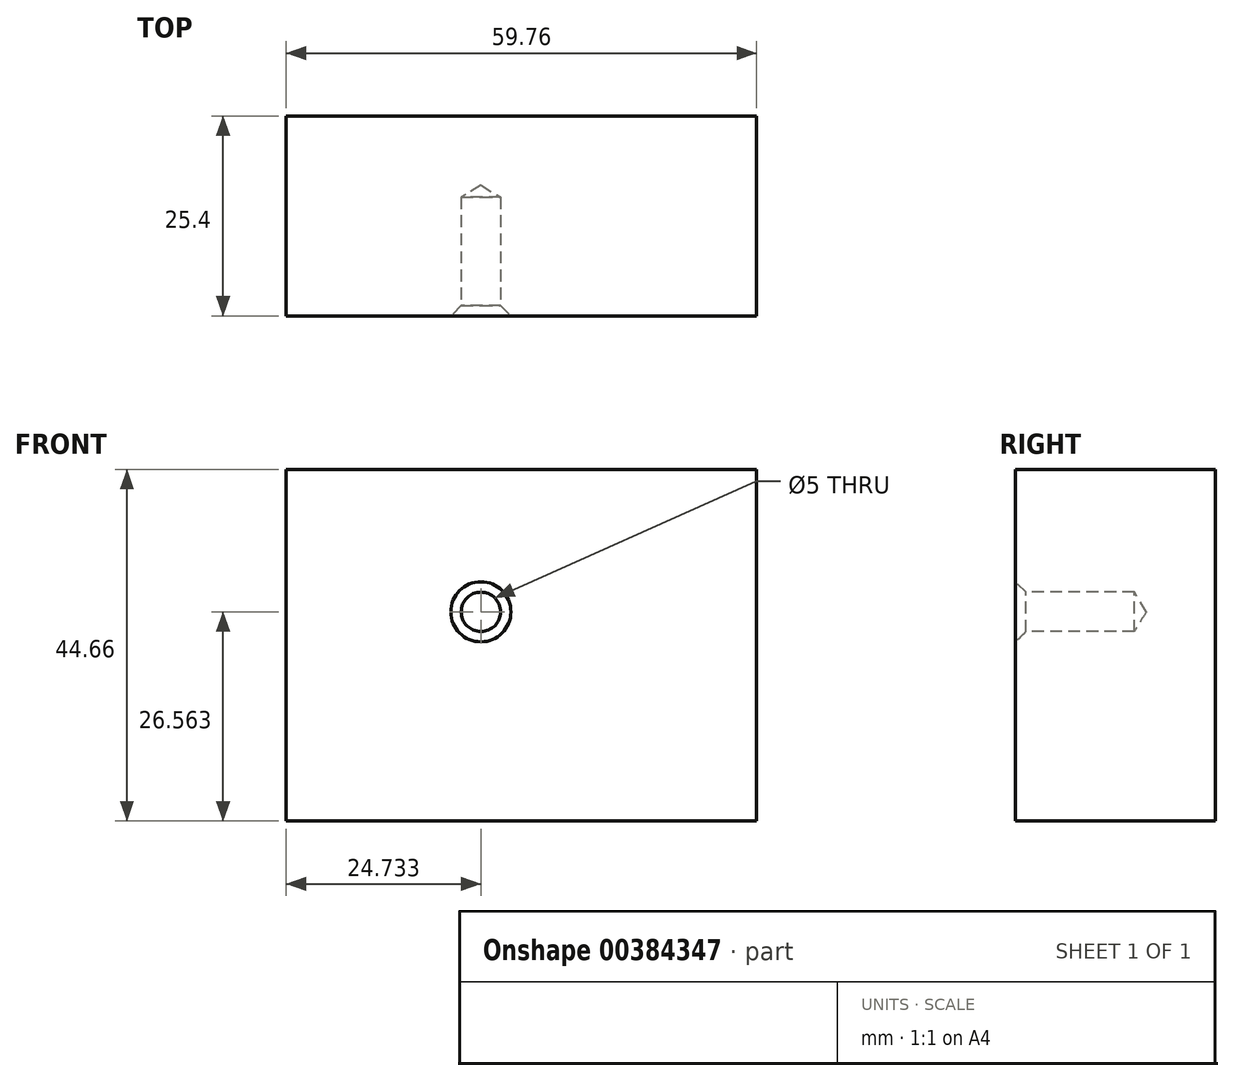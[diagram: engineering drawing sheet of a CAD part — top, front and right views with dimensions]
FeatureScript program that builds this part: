
annotation { "Feature Type Name" : "Feature", "Feature Type Description" : "" }
export const myFeature = defineFeature(function(context is Context, id is Id, definition is map)
    precondition{}
    {
        {
            var Q0;
            Q0=qCreatedBy(makeId("Front.planeOp"),FACE);
            var sketch = newSketch(context, id + "F0", { "sketchPlane" : qUnion([Q0])});
            skLineSegment(sketch, "E0.bottom", {"start": v(-85.82, 51.96) * mm, "end": v(-26.06, 51.96) * mm});
            skLineSegment(sketch, "E0.top", {"start": v(-85.82, 7.3) * mm, "end": v(-26.06, 7.3) * mm});
            skLineSegment(sketch, "E0.left", {"start": v(-85.82, 51.96) * mm, "end": v(-85.82, 7.3) * mm});
            skLineSegment(sketch, "E0.right", {"start": v(-26.06, 51.96) * mm, "end": v(-26.06, 7.3) * mm});
            skCircle(sketch, "E1", {"center": v(-61.09, 33.86) * mm, "radius": 5.53 * mm});
            skSolve(sketch);
        }
        {
            var Q0;
            Q0=makeQuery(id+"F0.imprint","IMPRINT",FACE,{"disambiguationData":[TD([[makeQuery(id+"F0.imprint","IMPRINT",EDGE,{"derivedFrom":sQuery(id+"F0.wireOp",EDGE,"E0.bottom")}),-1.0]])]});
            var Q1;
            Q1=makeQuery(id+"F0.imprint","IMPRINT",FACE,{"disambiguationData":[TD([[makeQuery(id+"F0.imprint","IMPRINT",EDGE,{"derivedFrom":sQuery(id+"F0.wireOp",EDGE,"E1")}),1.0]])]});
            extrude(context, id + "F1", {"entities" : qUnion([Q0, Q1]), "oppositeDirection" : true, "depth" : 25.4 * mm});
        }
        {
            var Q0;
            Q0=sQuery(id+"F0.wireOp",VERTEX,"E1.center");
            var Q1;
            Q1=makeQuery(id+"F1.opExtrude","SWEPT_BODY",BODY,{"disambiguationData":[OSD([sQuery(id+"F0.wireOp",EDGE,"E0.bottom"),sQuery(id+"F0.wireOp",EDGE,"E0.top"),sQuery(id+"F0.wireOp",EDGE,"E0.left"),sQuery(id+"F0.wireOp",EDGE,"E0.right")])]});
            hole(context, id + "F2", {"style" : HoleStyle.C_SINK, "endStyle" : HoleEndStyle.BLIND, "holeDiameter" : 5 * mm, "cSinkDiameter" : 7.62 * mm, "cSinkAngle" : 90 * degree, "holeDepth" : 15.1 * mm, "isTappedThrough" : true, "tappedDepth" : 12.7 * mm, "tapClearance" : 3, "startFromSketch" : true, "locations" : qUnion([Q0]), "scope" : qUnion([Q1])});
        }
    });
